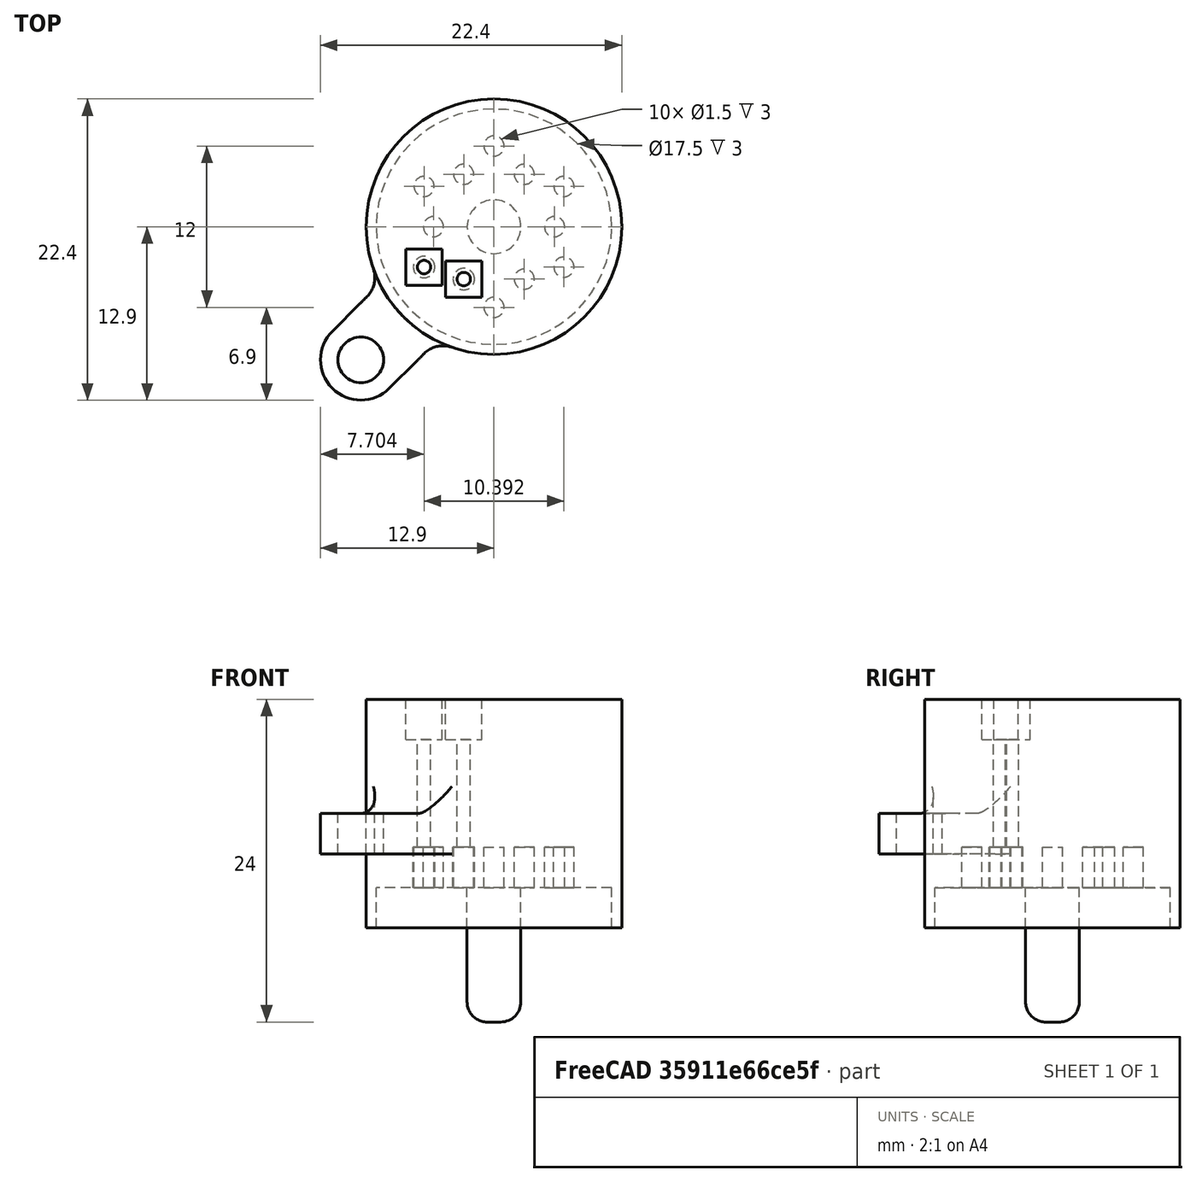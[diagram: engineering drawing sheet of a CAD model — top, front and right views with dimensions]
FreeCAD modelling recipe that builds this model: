
FCSTD DOCUMENT  (FreeCAD 0.18RUnknown)
Label: BasicProgrammerConnector
License: All rights reserved
LicenseURL: http://en.wikipedia.org/wiki/All_rights_reserved
objects: Part::Cylinder×11, PartDesign::FeatureBase×11, Part::Cut×4, Part::Box×3, Part::MultiFuse×3, Part::Compound×2, Part::Fillet×2, Part::Fuse×1, Part::FeaturePython×1, Mesh::Feature×1
note: 38 computed .brp shape members not serialized (recipe doc carries the construction recipe); baked Part::Feature solids carry a one-line shape summary decoded from their .brp

FEATURE [Part::Cylinder] Cylinder004
  Angle = 360
  AttacherType = Attacher::AttachEngine3D
  Height = 3
  Placement = pos=(0,6,0) rot=(0,0,1;0rad)
  Radius = 0.75
FEATURE [PartDesign::FeatureBase] Clone
  BaseFeature = -> Cylinder004
  Placement = pos=(-5.19615,3,0) rot=(0,0,1;1.0472rad)
FEATURE [PartDesign::FeatureBase] Clone001
  BaseFeature = -> Cylinder004
  Placement = pos=(-5.19615,-3,0) rot=(0,0,1;2.0944rad)
FEATURE [PartDesign::FeatureBase] Clone002
  BaseFeature = -> Cylinder004
  Placement = pos=(-7e-16,-6,0) rot=(0,0,1;3.14159rad)
FEATURE [PartDesign::FeatureBase] Clone003
  BaseFeature = -> Cylinder004
  Placement = pos=(5.19615,-3,0) rot=(0,0,1;4.18879rad)
FEATURE [PartDesign::FeatureBase] Clone004
  BaseFeature = -> Cylinder004
  Placement = pos=(5.19615,3,0) rot=(0,0,1;5.23599rad)
FEATURE [PartDesign::FeatureBase] Clone005
  BaseFeature = -> Cylinder004
  Placement = pos=(-2.25,3.89711,0) rot=(0,0,1;0.523599rad)
FEATURE [PartDesign::FeatureBase] Clone006
  BaseFeature = -> Cylinder004
  Placement = pos=(-4.5,1e-15,0) rot=(0,0,1;1.5708rad)
FEATURE [PartDesign::FeatureBase] Clone007
  BaseFeature = -> Cylinder004
  Placement = pos=(-2.25,-3.89711,0) rot=(0,0,1;2.61799rad)
FEATURE [PartDesign::FeatureBase] Clone008
  BaseFeature = -> Cylinder004
  Placement = pos=(2.25,-3.89711,0) rot=(0,0,1;3.66519rad)
FEATURE [PartDesign::FeatureBase] Clone009
  BaseFeature = -> Cylinder004
  Placement = pos=(4.5,-1e-15,0) rot=(0,0,1;4.71239rad)
FEATURE [PartDesign::FeatureBase] Clone010
  BaseFeature = -> Cylinder004
  Placement = pos=(2.25,3.89711,0) rot=(0,0,1;5.75959rad)
FEATURE [Part::Compound] Compound
  Links = -> [Cylinder004,Clone009,Clone007,Clone008,Clone003,Clone,Clone010,Clone001,Clone002,Clone004,Clone005,Clone006]
FEATURE [Part::Box] Box002  label="Cube002"
  AttacherType = Attacher::AttachEngine3D
  Height = 6
  Length = 2.7
  Placement = pos=(-1.35,-1.35,11) rot=(0,0,1;0rad)
  Width = 2.7
FEATURE [Part::Box] Box003  label="Cube003"
  AttacherType = Attacher::AttachEngine3D
  Height = 6
  Length = 2.7
  Placement = pos=(-1.35,-1.35,11) rot=(0,0,1;0rad)
  Width = 2.7
FEATURE [Part::Cylinder] Cylinder005
  Angle = 360
  AttacherType = Attacher::AttachEngine3D
  Height = 17
  Radius = 0.5
FEATURE [Part::Cylinder] Cylinder006
  Angle = 360
  AttacherType = Attacher::AttachEngine3D
  Height = 3
  Radius = 0.8
FEATURE [Part::MultiFuse] Fusion002  label="Pin Cutout002"
  Placement = pos=(-5.2,-3,0) rot=(0,0,1;0rad)
  Shapes = -> [Cylinder006,Cylinder005,Box003]
FEATURE [Part::Cylinder] Cylinder007
  Angle = 360
  AttacherType = Attacher::AttachEngine3D
  Height = 17
  Radius = 0.5
FEATURE [Part::Cylinder] Cylinder008
  Angle = 360
  AttacherType = Attacher::AttachEngine3D
  Height = 3
  Radius = 0.8
FEATURE [Part::MultiFuse] Fusion003  label="Pin Cutout003"
  Placement = pos=(-2.25,-3.9,0) rot=(0,0,1;0rad)
  Shapes = -> [Cylinder008,Cylinder007,Box002]
FEATURE [Part::Cylinder] Cylinder009
  Angle = 360
  AttacherType = Attacher::AttachEngine3D
  Height = 14
  Radius = 8.75
FEATURE [Part::Cut] Cut
  Base = -> Cylinder009
  Tool = -> Compound
FEATURE [Part::Compound] Compound001
  Links = -> [Fusion002,Fusion003]
FEATURE [Part::Cut] Cut001
  Base = -> Cut
  Tool = -> Compound001
FEATURE [Part::Cylinder] Cylinder010
  Angle = 360
  AttacherType = Attacher::AttachEngine3D
  Height = 17
  Placement = pos=(0,0,-3) rot=(0,0,1;0rad)
  Radius = 9.5
FEATURE [Part::Cylinder] Cylinder011
  Angle = 360
  AttacherType = Attacher::AttachEngine3D
  Height = 17
  Placement = pos=(0,0,-3) rot=(0,0,1;0rad)
  Radius = 8.75
FEATURE [Part::Cut] Cut002
  Base = -> Cylinder010
  Tool = -> Cylinder011
FEATURE [Part::Cylinder] Cylinder012
  Angle = 360
  AttacherType = Attacher::AttachEngine3D
  Height = 10
  Placement = pos=(0,0,-10) rot=(0,0,1;0rad)
  Radius = 2
FEATURE [Part::Fillet] Fillet
  Base = -> Cylinder012
  Edges = 1 edges r=1.5: [Edge3]
FEATURE [Part::Cylinder] Cylinder013
  Angle = 360
  AttacherType = Attacher::AttachEngine3D
  Height = 3
  Placement = pos=(0,14,2.5) rot=(0,0,1;0rad)
  Radius = 3
FEATURE [Part::Cylinder] Cylinder014
  Angle = 360
  AttacherType = Attacher::AttachEngine3D
  Height = 3
  Placement = pos=(0,14,2.5) rot=(0,0,1;0rad)
  Radius = 1.7
FEATURE [Part::Box] Box004  label="Cube004"
  AttacherType = Attacher::AttachEngine3D
  Height = 3
  Length = 6
  Placement = pos=(-3,8,2.5) rot=(0,0,1;0rad)
  Width = 6
FEATURE [Part::Fuse] Fusion004
  Base = -> Cylinder013
  Tool = -> Box004
FEATURE [Part::Cut] Cut003
  Base = -> Fusion004
  Placement = pos=(0,0,0) rot=(0,0,1;2.35619rad)
  Tool = -> Cylinder014
FEATURE [Part::FeaturePython] Connect  # WARN: FeaturePython — macro-defined, semantics opaque (R4)
  Objects = -> [Cut002,Cut003]
  Tolerance = 0
FEATURE [Part::Fillet] Fillet001
  Base = -> Connect
  Edges = 3 edges r=2: [Edge16,Edge17,Edge18]
FEATURE [Part::MultiFuse] Fusion005
  Shapes = -> [Cut001,Fillet,Fillet001]
FEATURE [Mesh::Feature] Mesh  label="Fusion005 (Meshed)"
